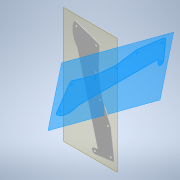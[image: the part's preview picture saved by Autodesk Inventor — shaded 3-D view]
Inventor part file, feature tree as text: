
AUTODESK INVENTOR PART (.ipt)
format: ipt  version: 2020 (Build 240168000, 168)  size: 145,920 bytes
history: native  units: mm
features: reference x6, other x5, plane x1, extrude x1, sketch x1
ambient origin geometry x8: Origin, YZ Plane, XZ Plane, XY Plane, X Axis, Y Axis, Z Axis, Center Point
bodies: Solid1 (feature_tree)
feature tree (14):
  plane  "Work Plane1"
  extrude  "Extrusion1"  [1 undecoded]
  sketch  "Sketch1"  dims[d0=1.0mm d1=0.0mm]
  reference  "Reference1"
  reference  "Reference2"
  reference  "Reference3"
  reference  "Reference4"
  reference  "Reference5"
  reference  "Reference6"
  other  "Kauri Assembly.iam"
  other  "Kauri side plate:2"
  other  "Kauri mid plate v2:1"
  other  "Kauri arm disc aero:1"
  other  "Kauri arm long disc aero:2"
note: 1 required parameter value undecoded (feature->parameter linkage not recoverable at this tier; creation-order binding heuristic only, values carry confidence <= 0.55)
